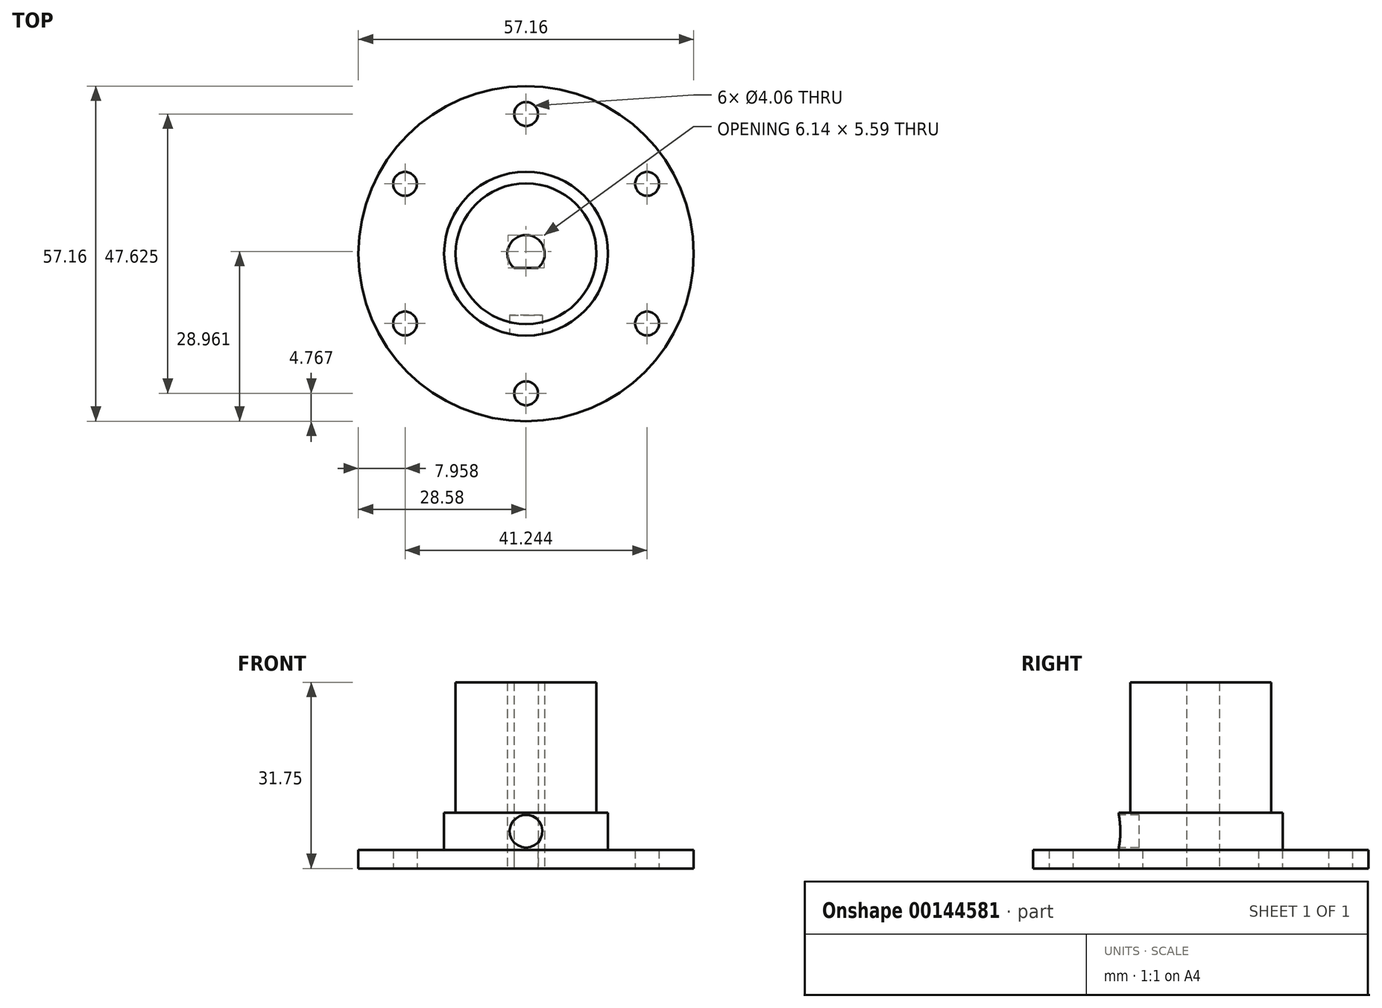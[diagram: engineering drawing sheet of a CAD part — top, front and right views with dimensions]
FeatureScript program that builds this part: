
annotation { "Feature Type Name" : "Feature", "Feature Type Description" : "" }
export const myFeature = defineFeature(function(context is Context, id is Id, definition is map)
    precondition{}
    {
        {
            var Q0;
            Q0=qCreatedBy(makeId("Top.planeOp"),FACE);
            var sketch = newSketch(context, id + "F0", { "sketchPlane" : qUnion([Q0])});
            skCircle(sketch, "E0", {"center": v(0, 0) * mm, "radius": 28.58 * mm});
            skPoint(sketch, "E1", {"position": v(0, 23.81) * mm});
            skCircle(sketch, "E2", {"center": v(0, 23.81) * mm, "radius": 2.03 * mm});
            skPoint(sketch, "E3.1.0", {"position": v(-20.62, -11.9) * mm});
            skPoint(sketch, "E3.2.0", {"position": v(20.62, -11.9) * mm});
            skCircle(sketch, "E4.1.0", {"center": v(-20.62, 11.9) * mm, "radius": 2.03 * mm});
            skCircle(sketch, "E4.2.0", {"center": v(-20.62, -11.9) * mm, "radius": 2.03 * mm});
            skCircle(sketch, "E4.3.0", {"center": v(0, -23.81) * mm, "radius": 2.03 * mm});
            skCircle(sketch, "E4.4.0", {"center": v(20.62, -11.9) * mm, "radius": 2.03 * mm});
            skCircle(sketch, "E4.5.0", {"center": v(20.62, 11.9) * mm, "radius": 2.03 * mm});
            skSolve(sketch);
        }
        {
            var Q0;
            Q0=makeQuery(id+"F0.imprint","IMPRINT",FACE,{"disambiguationData":[TD([[makeQuery(id+"F0.imprint","IMPRINT",EDGE,{"derivedFrom":sQuery(id+"F0.wireOp",EDGE,"E0")}),1.0]])]});
            extrude(context, id + "F1", {"entities" : qUnion([Q0]), "depth" : 3.17 * mm});
        }
        {
            var Q0;
            Q0=makeQuery(id+"F1.opExtrude","CAP_FACE",FACE,{"disambiguationData":[OSD([sQuery(id+"F0.wireOp",EDGE,"E0"),sQuery(id+"F0.wireOp",EDGE,"E2"),sQuery(id+"F0.wireOp",EDGE,"E4.1.0"),sQuery(id+"F0.wireOp",EDGE,"E4.2.0"),sQuery(id+"F0.wireOp",EDGE,"E4.3.0"),sQuery(id+"F0.wireOp",EDGE,"E4.4.0"),sQuery(id+"F0.wireOp",EDGE,"E4.5.0")])],"isStart":false});
            var sketch = newSketch(context, id + "F2", { "sketchPlane" : qUnion([Q0])});
            skCircle(sketch, "E5", {"center": v(0, 0) * mm, "radius": 13.97 * mm});
            skSolve(sketch);
        }
        {
            var Q0;
            Q0=makeQuery(id+"F2.imprint","IMPRINT",FACE,{"disambiguationData":[TD([[makeQuery(id+"F2.imprint","IMPRINT",EDGE,{"derivedFrom":sQuery(id+"F2.wireOp",EDGE,"E5")}),1.0]])]});
            extrude(context, id + "F3", {"entities" : qUnion([Q0]), "operationType" : NewBodyOperationType.ADD, "depth" : 6.35 * mm});
        }
        {
            var Q0;
            Q0=makeQuery(id+"F3.opExtrude","CAP_FACE",FACE,{"disambiguationData":[OSD([sQuery(id+"F2.wireOp",EDGE,"E5")])],"isStart":false});
            var sketch = newSketch(context, id + "F4", { "sketchPlane" : qUnion([Q0])});
            skCircle(sketch, "E6", {"center": v(0, 0) * mm, "radius": 12 * mm});
            skSolve(sketch);
        }
        {
            var Q0;
            Q0=makeQuery(id+"F4.imprint","IMPRINT",FACE,{"disambiguationData":[TD([[makeQuery(id+"F4.imprint","IMPRINT",EDGE,{"derivedFrom":sQuery(id+"F4.wireOp",EDGE,"E6")}),1.0]])]});
            extrude(context, id + "F5", {"entities" : qUnion([Q0]), "operationType" : NewBodyOperationType.ADD, "depth" : 22.22 * mm});
        }
        {
            var Q0;
            Q0=makeQuery(id+"F1.opExtrude","CAP_FACE",FACE,{"disambiguationData":[OSD([sQuery(id+"F0.wireOp",EDGE,"E0"),sQuery(id+"F0.wireOp",EDGE,"E2"),sQuery(id+"F0.wireOp",EDGE,"E4.1.0"),sQuery(id+"F0.wireOp",EDGE,"E4.2.0"),sQuery(id+"F0.wireOp",EDGE,"E4.3.0"),sQuery(id+"F0.wireOp",EDGE,"E4.4.0"),sQuery(id+"F0.wireOp",EDGE,"E4.5.0")])],"isStart":true});
            var sketch = newSketch(context, id + "F6", { "sketchPlane" : qUnion([Q0])});
            skCircle(sketch, "E7", {"center": v(0, 0) * mm, "radius": 3.18 * mm});
            skLineSegment(sketch, "E8", {"start": v(0, 2.41) * mm, "end": v(-2.06, 2.41) * mm});
            skLineSegment(sketch, "E9", {"start": v(-2.06, 2.41) * mm, "end": v(2.06, 2.41) * mm});
            skSolve(sketch);
        }
        {
            var Q0;
            {var subQ0=sQuery(id+"F6.wireOp",EDGE,"E9");var subQ4=makeQuery(id+"F6.imprint","IMPRINT",VERTEX,{"derivedFrom":subQ0});Q0=makeQuery(id+"F6.imprint","IMPRINT",FACE,{"disambiguationData":[TD([[makeQuery(id+"F6.imprint","IMPRINT",EDGE,{"disambiguationData":[TD([[subQ4,1.0]])],"derivedFrom":subQ0}),-1.0]])]});}
            extrude(context, id + "F7", {"entities" : qUnion([Q0]), "operationType" : NewBodyOperationType.REMOVE, "endBound" : BoundingType.UP_TO_NEXT, "oppositeDirection" : true, "depth" : 25.4 * mm});
        }
        {
            var Q0;
            Q0=qCreatedBy(makeId("Front.planeOp"),FACE);
            cPlane(context, id + "F8", {"entities" : qUnion([Q0]), "cplaneType" : CPlaneType.OFFSET, "offset" : 14.29 * mm, "width" : 152.4 * mm, "height" : 152.4 * mm});
        }
        {
            var Q0;
            Q0=qCreatedBy(id+"F8.planeOp",FACE);
            var sketch = newSketch(context, id + "F9", { "sketchPlane" : qUnion([Q0])});
            skCircle(sketch, "E10", {"center": v(0, 6.35) * mm, "radius": 1.42 * mm});
            skSolve(sketch);
        }
        {
            var Q0;
            Q0=makeQuery(id+"F9.imprint","IMPRINT",FACE,{"disambiguationData":[TD([[makeQuery(id+"F9.imprint","IMPRINT",EDGE,{"derivedFrom":sQuery(id+"F9.wireOp",EDGE,"E10")}),1.0]])]});
            extrude(context, id + "F10", {"entities" : qUnion([Q0]), "operationType" : NewBodyOperationType.REMOVE, "endBound" : BoundingType.UP_TO_NEXT, "oppositeDirection" : true, "depth" : 25.4 * mm});
        }
        {
            var Q0;
            Q0=qCreatedBy(id+"F8.planeOp",FACE);
            var sketch = newSketch(context, id + "F11", { "sketchPlane" : qUnion([Q0])});
            skCircle(sketch, "E11", {"center": v(0, 6.35) * mm, "radius": 2.8 * mm});
            skSolve(sketch);
        }
        {
            var Q0;
            Q0=makeQuery(id+"F11.imprint","IMPRINT",FACE,{"disambiguationData":[TD([[makeQuery(id+"F11.imprint","IMPRINT",EDGE,{"derivedFrom":sQuery(id+"F11.wireOp",EDGE,"E11")}),1.0]])]});
            extrude(context, id + "F12", {"entities" : qUnion([Q0]), "operationType" : NewBodyOperationType.REMOVE, "oppositeDirection" : true, "depth" : 3.8 * mm});
        }
    });
